# Revit family: Скамейка чугунная «Ампир»
name_source: partatom
category: Антураж
revit_build: Autodesk Revit 2017 (Build: 20160225_1515(x64)
units: mm (PartAtom-declared; Revit-internal decimal feet)

## family parameters
Всегда вертикально = Да
Источник визуального образа = Геометрия семейства
На основе рабочей плоскости = Нет
Общий = Нет
При загрузке вырезать с полостями = Нет
Точка расчета площади = Нет

## types (4) — shared parameters
ADSK_Код изделия = 9084
ADSK_Материал доски = Лиственница
ADSK_Материал опоры = Чугун, серый
ADSK_Материал фурнитуры = Чугун, серый
ADSK_Наименование = Скамейка чугунная «Ампир»
ADSK_Размер_Высота = 930 мм
ADSK_Размер_Ширина = 620 мм
URL = https://hobbyka.ru
Изготовитель = ООО "Хоббика"
zero-valued in all types: Высота

## per-type parameters (varying)
| type | ADSK_Размер_Длина | Длина доски | Стоимость | Центральная опора |
| Скамейка чугунная «Ампир» 1,5м | 1500 мм | 1442 мм | 18260 $ | Нет |
| Скамейка чугунная «Ампир» 1,8м | 1800 мм | 1742 мм | 19066 $ | Нет |
| Скамейка чугунная «Ампир» 2,0м (3 опоры) | 2000 мм | 1942 мм | 25911 $ | Да |
| Скамейка чугунная «Ампир» 3,0м | 3000 мм | 2942 мм | 28598 $ | Да |
